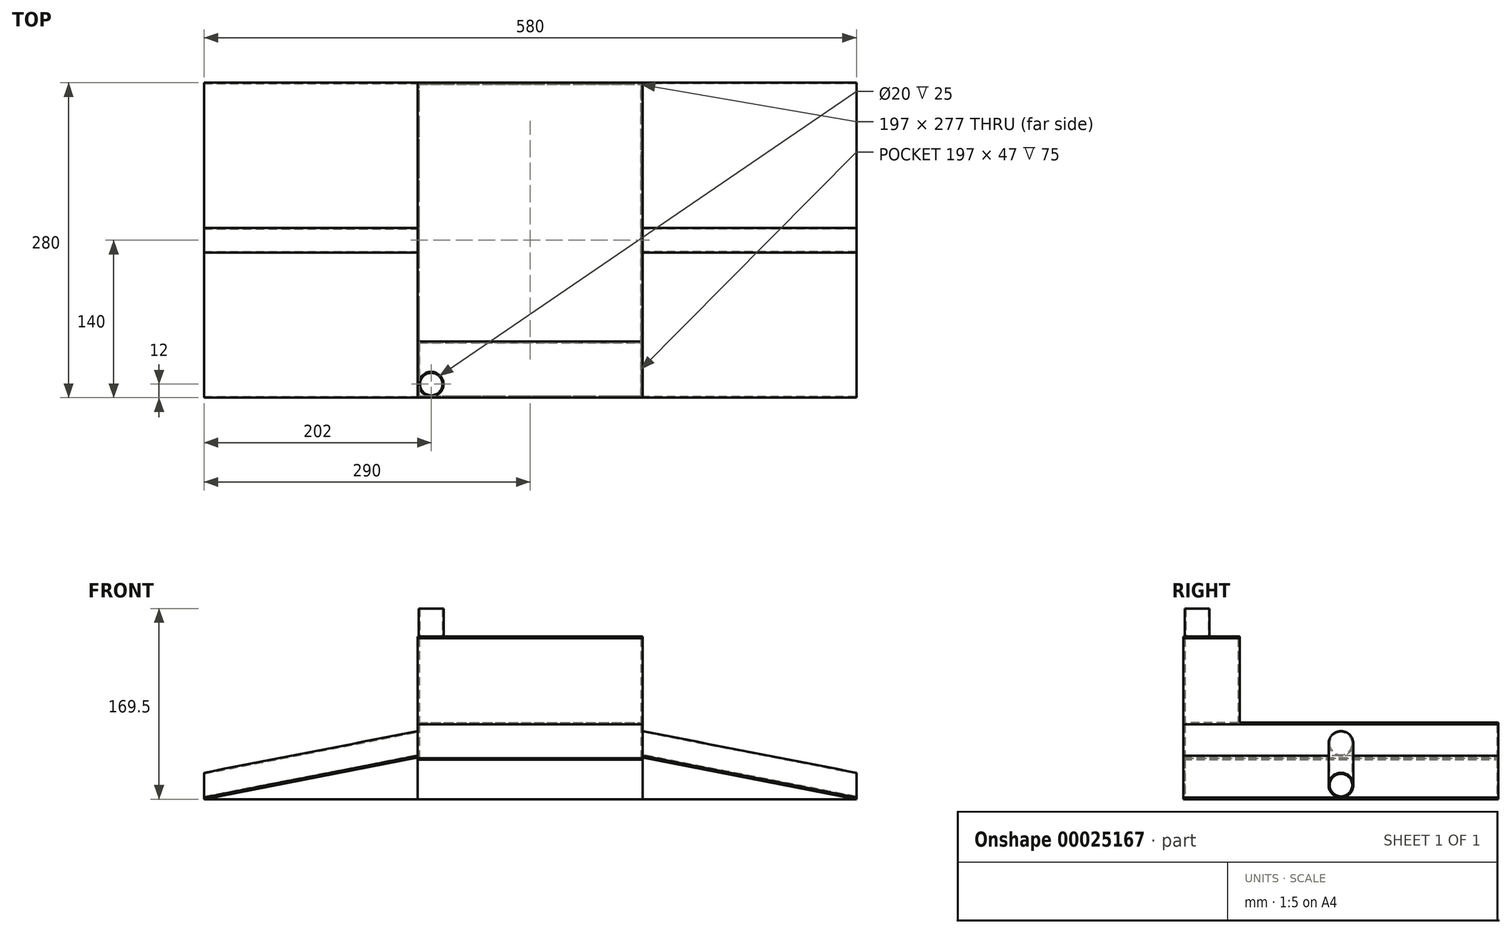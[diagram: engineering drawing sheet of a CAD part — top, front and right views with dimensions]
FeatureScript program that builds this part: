
annotation { "Feature Type Name" : "Feature", "Feature Type Description" : "" }
export const myFeature = defineFeature(function(context is Context, id is Id, definition is map)
    precondition{}
    {
        {
            var Q0;
            Q0=qCreatedBy(makeId("Top.planeOp"),FACE);
            var sketch = newSketch(context, id + "F0", { "sketchPlane" : qUnion([Q0])});
            skLineSegment(sketch, "E0.bottom", {"start": v(0, 0) * mm, "end": v(200, 0) * mm});
            skLineSegment(sketch, "E0.top", {"start": v(0, 280) * mm, "end": v(200, 280) * mm});
            skLineSegment(sketch, "E0.left", {"start": v(0, 0) * mm, "end": v(0, 280) * mm});
            skLineSegment(sketch, "E0.right", {"start": v(200, 0) * mm, "end": v(200, 280) * mm});
            skLineSegment(sketch, "E1.bottom", {"start": v(1.5, 278.5) * mm, "end": v(198.5, 278.5) * mm});
            skLineSegment(sketch, "E1.top", {"start": v(1.5, 1.5) * mm, "end": v(198.5, 1.5) * mm});
            skLineSegment(sketch, "E1.left", {"start": v(1.5, 278.5) * mm, "end": v(1.5, 1.5) * mm});
            skLineSegment(sketch, "E1.right", {"start": v(198.5, 278.5) * mm, "end": v(198.5, 1.5) * mm});
            skSolve(sketch);
        }
        {
            var Q0;
            Q0=makeQuery(id+"F0.imprint","IMPRINT",FACE,{"disambiguationData":[TD([[makeQuery(id+"F0.imprint","IMPRINT",EDGE,{"derivedFrom":sQuery(id+"F0.wireOp",EDGE,"E0.bottom")}),1.0]])]});
            extrude(context, id + "F1", {"entities" : qUnion([Q0]), "depth" : 35 * mm});
        }
        {
            var Q0;
            Q0=makeQuery(id+"F1.opExtrude","CAP_FACE",FACE,{"disambiguationData":[OSD([sQuery(id+"F0.wireOp",EDGE,"E0.bottom"),sQuery(id+"F0.wireOp",EDGE,"E0.top"),sQuery(id+"F0.wireOp",EDGE,"E0.left"),sQuery(id+"F0.wireOp",EDGE,"E0.right"),sQuery(id+"F0.wireOp",EDGE,"E1.bottom"),sQuery(id+"F0.wireOp",EDGE,"E1.top"),sQuery(id+"F0.wireOp",EDGE,"E1.left"),sQuery(id+"F0.wireOp",EDGE,"E1.right")])],"isStart":false});
            var sketch = newSketch(context, id + "F2", { "sketchPlane" : qUnion([Q0])});
            skLineSegment(sketch, "E2.bottom", {"start": v(0, 0) * mm, "end": v(200, 0) * mm});
            skLineSegment(sketch, "E2.top", {"start": v(0, 280) * mm, "end": v(200, 280) * mm});
            skLineSegment(sketch, "E2.left", {"start": v(0, 0) * mm, "end": v(0, 280) * mm});
            skLineSegment(sketch, "E2.right", {"start": v(200, 0) * mm, "end": v(200, 280) * mm});
            skSolve(sketch);
        }
        {
            var Q0;
            Q0=makeQuery(id+"F2.imprint","IMPRINT",FACE,{"disambiguationData":[TD([[makeQuery(id+"F2.imprint","IMPRINT",EDGE,{"derivedFrom":makeQuery(id+"F1.opExtrude","CAP_EDGE",EDGE,{"disambiguationData":[OSD([sQuery(id+"F0.wireOp",EDGE,"E1.bottom")])],"isStart":false})}),-1.0]])]});
            var Q1;
            Q1=makeQuery(id+"F2.imprint","IMPRINT",FACE,{"disambiguationData":[TD([[makeQuery(id+"F2.imprint","IMPRINT",EDGE,{"derivedFrom":sQuery(id+"F2.wireOp",EDGE,"E2.bottom")}),1.0]])]});
            extrude(context, id + "F3", {"entities" : qUnion([Q0, Q1]), "depth" : 1.5 * mm});
        }
        {
            var Q0;
            Q0=makeQuery(id+"F3.opExtrude","CAP_FACE",FACE,{"disambiguationData":[OSD([sQuery(id+"F2.wireOp",EDGE,"E2.bottom"),sQuery(id+"F2.wireOp",EDGE,"E2.top"),sQuery(id+"F2.wireOp",EDGE,"E2.left"),sQuery(id+"F2.wireOp",EDGE,"E2.right")])],"isStart":false});
            var sketch = newSketch(context, id + "F4", { "sketchPlane" : qUnion([Q0])});
            skLineSegment(sketch, "E3.bottom", {"start": v(200, 280) * mm, "end": v(0, 280) * mm});
            skLineSegment(sketch, "E3.top", {"start": v(200, 0) * mm, "end": v(0, 0) * mm});
            skLineSegment(sketch, "E3.left", {"start": v(200, 280) * mm, "end": v(200, 0) * mm});
            skLineSegment(sketch, "E3.right", {"start": v(0, 280) * mm, "end": v(0, 0) * mm});
            skLineSegment(sketch, "E4.bottom", {"start": v(1.5, 1.5) * mm, "end": v(198.5, 1.5) * mm});
            skLineSegment(sketch, "E4.top", {"start": v(1.5, 278.5) * mm, "end": v(198.5, 278.5) * mm});
            skLineSegment(sketch, "E4.left", {"start": v(1.5, 1.5) * mm, "end": v(1.5, 278.5) * mm});
            skLineSegment(sketch, "E4.right", {"start": v(198.5, 1.5) * mm, "end": v(198.5, 278.5) * mm});
            skSolve(sketch);
        }
        {
            var Q0;
            Q0 = qSketchRegion(id + "F4", true);
            extrude(context, id + "F5", {"entities" : qUnion([Q0]), "depth" : 30 * mm});
        }
        {
            var Q0;
            Q0=makeQuery(id+"F5.opExtrude","SWEPT_FACE",FACE,{"disambiguationData":[OSD([sQuery(id+"F4.wireOp",EDGE,"E3.right")])]});
            var sketch = newSketch(context, id + "F6", { "sketchPlane" : qUnion([Q0])});
            skLineSegment(sketch, "E5", {"start": v(-140, 36.5) * mm, "end": v(-140, 49.5) * mm});
            skCircle(sketch, "E6", {"center": v(-140, 49.5) * mm, "radius": 11 * mm});
            skCircle(sketch, "E7", {"center": v(-140, 49.5) * mm, "radius": 10 * mm});
            skSolve(sketch);
        }
        {
            var Q0;
            Q0=qCreatedBy(makeId("Front.planeOp"),FACE);
            cPlane(context, id + "F7", {"entities" : qUnion([Q0]), "cplaneType" : CPlaneType.OFFSET, "offset" : 140 * mm, "oppositeDirection" : true, "width" : 150 * mm, "height" : 150 * mm});
        }
        {
            var Q0;
            Q0=qCreatedBy(id+"F7.planeOp",FACE);
            var sketch = newSketch(context, id + "F8", { "sketchPlane" : qUnion([Q0])});
            skLineSegment(sketch, "E8", {"start": v(0, 0) * mm, "end": v(0, 49.5) * mm});
            skLineSegment(sketch, "E9", {"start": v(0, 49.5) * mm, "end": v(-190, 12.5) * mm});
            skLineSegment(sketch, "E10", {"start": v(-190, 12.5) * mm, "end": v(-10, 47.55) * mm});
            skSolve(sketch);
        }
        {
            var Q0;
            Q0=makeQuery(id+"F6.imprint","IMPRINT",FACE,{"disambiguationData":[TD([[makeQuery(id+"F6.imprint","IMPRINT",EDGE,{"derivedFrom":sQuery(id+"F6.wireOp",EDGE,"E6")}),1.0]])]});
            var Q1;
            Q1=sQuery(id+"F8.wireOp",EDGE,"E9");
            sweep(context, id + "F9", {"profiles" : qUnion([Q0]), "path" : qUnion([Q1])});
        }
        {
            var Q0;
            Q0=makeQuery(id+"F9.opSweep","CAP_FACE",FACE,{"disambiguationData":[OSD([sQuery(id+"F6.wireOp",EDGE,"E6"),sQuery(id+"F6.wireOp",EDGE,"E7"),sQuery(id+"F8.wireOp",VERTEX,"E9.end")])],"isStart":false});
            var sketch = newSketch(context, id + "F10", { "sketchPlane" : qUnion([Q0])});
            skLineSegment(sketch, "E11.bottom", {"start": v(-140, 1.5) * mm, "end": v(0, 1.5) * mm});
            skLineSegment(sketch, "E11.top", {"start": v(-140, 0) * mm, "end": v(0, 0) * mm});
            skLineSegment(sketch, "E11.right", {"start": v(0, 1.5) * mm, "end": v(0, 0) * mm});
            skLineSegment(sketch, "E12.bottom", {"start": v(-140, 1.5) * mm, "end": v(-280, 1.5) * mm});
            skLineSegment(sketch, "E12.top", {"start": v(-140, 0) * mm, "end": v(-280, 0) * mm});
            skLineSegment(sketch, "E12.right", {"start": v(-280, 1.5) * mm, "end": v(-280, 0) * mm});
            skSolve(sketch);
        }
        {
            var Q0;
            Q0=makeQuery(id+"F10.imprint","IMPRINT",FACE,{"disambiguationData":[TD([[makeQuery(id+"F10.imprint","IMPRINT",EDGE,{"derivedFrom":sQuery(id+"F10.wireOp",EDGE,"E11.bottom")}),-1.0]])]});
            var Q1;
            Q1=sQuery(id+"F8.wireOp",EDGE,"E9");
            sweep(context, id + "F11", {"profiles" : qUnion([Q0]), "path" : qUnion([Q1])});
        }
        {
            var Q0;
            Q0=qCreatedBy(makeId("Right.planeOp"),FACE);
            cPlane(context, id + "F12", {"entities" : qUnion([Q0]), "cplaneType" : CPlaneType.OFFSET, "offset" : 100 * mm, "width" : 150 * mm, "height" : 150 * mm});
        }
        {
            var Q0;
            Q0=makeQuery(id+"F11.opSweep","SWEPT_BODY",BODY,{"disambiguationData":[OSD([sQuery(id+"F6.wireOp",EDGE,"E6"),sQuery(id+"F8.wireOp",VERTEX,"E9.end"),sQuery(id+"F8.wireOp",EDGE,"E9"),sQuery(id+"F10.wireOp",EDGE,"bbc44509-5c85-48de-a6ec-72a2609fa2f3"),sQuery(id+"F10.wireOp",EDGE,"a9bd47df-7b8e-4d3d-8cbc-6e7aad29a798"),sQuery(id+"F10.wireOp",EDGE,"b129ef78-7b1a-4f70-9433-c68172c07502")])]});
            var Q1;
            Q1=makeQuery(id+"F9.opSweep","SWEPT_BODY",BODY,{"disambiguationData":[OSD([sQuery(id+"F6.wireOp",EDGE,"E6"),sQuery(id+"F6.wireOp",EDGE,"E7"),sQuery(id+"F8.wireOp",EDGE,"E9")])]});
            var Q2;
            Q2=makeQuery(id+"F11.opSweep","SWEPT_BODY",BODY,{"disambiguationData":[OSD([sQuery(id+"F6.wireOp",EDGE,"E6"),sQuery(id+"F8.wireOp",VERTEX,"E9.end"),sQuery(id+"F8.wireOp",EDGE,"E9"),sQuery(id+"F10.wireOp",EDGE,"c09ad4ab-e0c7-4d02-b4d3-9f80001b407e"),sQuery(id+"F10.wireOp",EDGE,"19dc77f5-9d7f-4f5a-aac5-f32d7d39baf3"),sQuery(id+"F10.wireOp",EDGE,"af366fa5-4e77-486b-961f-37b205b3a81b"),sQuery(id+"F10.wireOp",EDGE,"1364792c-ecac-41d2-8e04-122f8f5d8162")])]});
            var Q3;
            Q3=qCreatedBy(id+"F12.planeOp",FACE);
            mirror(context, id + "F13", {"entities" : qUnion([Q0, Q1, Q2]), "mirrorPlane" : qUnion([Q3])});
        }
        {
            var Q0;
            Q0=makeQuery(id+"F11.opSweep","SWEPT_FACE",FACE,{"disambiguationData":[OSD([sQuery(id+"F8.wireOp",EDGE,"E9"),sQuery(id+"F10.wireOp",EDGE,"E11.right")])]});
            var sketch = newSketch(context, id + "F14", { "sketchPlane" : qUnion([Q0])});
            skLineSegment(sketch, "E13", {"start": v(0, 37) * mm, "end": v(0, 0) * mm});
            skLineSegment(sketch, "E14", {"start": v(0, 0) * mm, "end": v(-190, 0) * mm});
            skLineSegment(sketch, "E15", {"start": v(-190, 0) * mm, "end": v(0, 37) * mm});
            skSolve(sketch);
        }
        {
            var Q0;
            Q0 = qSketchRegion(id + "F14", true);
            extrude(context, id + "F15", {"entities" : qUnion([Q0]), "oppositeDirection" : true, "depth" : 1 * mm});
        }
        {
            var Q0;
            Q0=makeQuery(id+"F15.opExtrude","SWEPT_BODY",BODY,{"disambiguationData":[OSD([sQuery(id+"F14.wireOp",EDGE,"E13"),sQuery(id+"F14.wireOp",EDGE,"E14"),sQuery(id+"F14.wireOp",EDGE,"E15")])]});
            var Q1;
            Q1=qCreatedBy(id+"F7.planeOp",FACE);
            mirror(context, id + "F16", {"entities" : qUnion([Q0]), "mirrorPlane" : qUnion([Q1])});
        }
        {
            var Q0;
            Q0=makeQuery(id+"F15.opExtrude","SWEPT_BODY",BODY,{"disambiguationData":[OSD([sQuery(id+"F14.wireOp",EDGE,"E13"),sQuery(id+"F14.wireOp",EDGE,"E14"),sQuery(id+"F14.wireOp",EDGE,"E15")])]});
            var Q1;
            Q1=makeQuery(id+"F16.opPattern","COPY",BODY,{"derivedFrom":makeQuery(id+"F15.opExtrude","SWEPT_BODY",BODY,{"disambiguationData":[OSD([sQuery(id+"F14.wireOp",EDGE,"E13"),sQuery(id+"F14.wireOp",EDGE,"E14"),sQuery(id+"F14.wireOp",EDGE,"E15")])]}),"instanceName":"1"});
            var Q2;
            Q2=qCreatedBy(id+"F12.planeOp",FACE);
            mirror(context, id + "F17", {"entities" : qUnion([Q0, Q1]), "mirrorPlane" : qUnion([Q2])});
        }
        {
            var Q0;
            Q0=makeQuery(id+"F1.opExtrude","CAP_FACE",FACE,{"disambiguationData":[OSD([sQuery(id+"F0.wireOp",EDGE,"E0.bottom"),sQuery(id+"F0.wireOp",EDGE,"E0.top"),sQuery(id+"F0.wireOp",EDGE,"E0.left"),sQuery(id+"F0.wireOp",EDGE,"E0.right"),sQuery(id+"F0.wireOp",EDGE,"E1.bottom"),sQuery(id+"F0.wireOp",EDGE,"E1.top"),sQuery(id+"F0.wireOp",EDGE,"E1.left"),sQuery(id+"F0.wireOp",EDGE,"E1.right")])],"isStart":true});
            var sketch = newSketch(context, id + "F18", { "sketchPlane" : qUnion([Q0])});
            skLineSegment(sketch, "E16", {"start": v(198.5, -278.5) * mm, "end": v(200, -278.5) * mm});
            skLineSegment(sketch, "E17", {"start": v(1.5, -278.5) * mm, "end": v(0, -278.5) * mm});
            skLineSegment(sketch, "E18", {"start": v(198.5, -1.5) * mm, "end": v(200, -1.5) * mm});
            skLineSegment(sketch, "E19", {"start": v(1.5, -1.5) * mm, "end": v(0, -1.5) * mm});
            skSolve(sketch);
        }
        {
            var Q0;
            {var subQ2=sQuery(id+"F18.wireOp",EDGE,"E16");Q0=makeQuery(id+"F18.imprint","IMPRINT",FACE,{"disambiguationData":[TD([[makeQuery(id+"F18.imprint","IMPRINT",EDGE,{"derivedFrom":subQ2}),1.0]])]});}
            var Q1;
            {var subQ2=sQuery(id+"F18.wireOp",EDGE,"E17");Q1=makeQuery(id+"F18.imprint","IMPRINT",FACE,{"disambiguationData":[TD([[makeQuery(id+"F18.imprint","IMPRINT",EDGE,{"derivedFrom":subQ2}),-1.0]])]});}
            extrude(context, id + "F19", {"entities" : qUnion([Q0, Q1]), "operationType" : NewBodyOperationType.REMOVE, "oppositeDirection" : true, "depth" : 35 * mm});
        }
        {
            var Q0;
            Q0=makeQuery(id+"F5.opExtrude","CAP_FACE",FACE,{"disambiguationData":[OSD([sQuery(id+"F4.wireOp",EDGE,"E3.bottom"),sQuery(id+"F4.wireOp",EDGE,"E3.top"),sQuery(id+"F4.wireOp",EDGE,"E3.left"),sQuery(id+"F4.wireOp",EDGE,"E3.right"),sQuery(id+"F4.wireOp",EDGE,"E4.bottom"),sQuery(id+"F4.wireOp",EDGE,"E4.top"),sQuery(id+"F4.wireOp",EDGE,"E4.left"),sQuery(id+"F4.wireOp",EDGE,"E4.right")])],"isStart":false});
            var sketch = newSketch(context, id + "F20", { "sketchPlane" : qUnion([Q0])});
            skLineSegment(sketch, "E20.bottom", {"start": v(200, 280) * mm, "end": v(0, 280) * mm});
            skLineSegment(sketch, "E20.top", {"start": v(200, 0) * mm, "end": v(0, 0) * mm});
            skLineSegment(sketch, "E20.left", {"start": v(200, 280) * mm, "end": v(200, 0) * mm});
            skLineSegment(sketch, "E20.right", {"start": v(0, 280) * mm, "end": v(0, 0) * mm});
            skSolve(sketch);
        }
        {
            var Q0;
            Q0=makeQuery(id+"F20.imprint","IMPRINT",FACE,{"disambiguationData":[TD([[makeQuery(id+"F20.imprint","IMPRINT",EDGE,{"derivedFrom":makeQuery(id+"F5.opExtrude","CAP_EDGE",EDGE,{"disambiguationData":[OSD([sQuery(id+"F4.wireOp",EDGE,"E4.bottom")])],"isStart":false})}),1.0]])]});
            var Q1;
            Q1=makeQuery(id+"F20.imprint","IMPRINT",FACE,{"disambiguationData":[TD([[makeQuery(id+"F20.imprint","IMPRINT",EDGE,{"derivedFrom":sQuery(id+"F20.wireOp",EDGE,"E20.bottom")}),-1.0]])]});
            extrude(context, id + "F21", {"entities" : qUnion([Q0, Q1]), "depth" : 1.5 * mm});
        }
        {
            var Q0;
            Q0=makeQuery(id+"F21.opExtrude","CAP_FACE",FACE,{"disambiguationData":[OSD([sQuery(id+"F20.wireOp",EDGE,"E20.bottom"),sQuery(id+"F20.wireOp",EDGE,"E20.top"),sQuery(id+"F20.wireOp",EDGE,"E20.left"),sQuery(id+"F20.wireOp",EDGE,"E20.right")])],"isStart":false});
            var sketch = newSketch(context, id + "F22", { "sketchPlane" : qUnion([Q0])});
            skLineSegment(sketch, "E21.bottom", {"start": v(0, 0) * mm, "end": v(200, 0) * mm});
            skLineSegment(sketch, "E21.top", {"start": v(0, 50) * mm, "end": v(200, 50) * mm});
            skLineSegment(sketch, "E21.left", {"start": v(0, 0) * mm, "end": v(0, 50) * mm});
            skLineSegment(sketch, "E21.right", {"start": v(200, 0) * mm, "end": v(200, 50) * mm});
            skLineSegment(sketch, "E22.bottom", {"start": v(1.5, 48.5) * mm, "end": v(198.5, 48.5) * mm});
            skLineSegment(sketch, "E22.top", {"start": v(1.5, 1.5) * mm, "end": v(198.5, 1.5) * mm});
            skLineSegment(sketch, "E22.left", {"start": v(1.5, 48.5) * mm, "end": v(1.5, 1.5) * mm});
            skLineSegment(sketch, "E22.right", {"start": v(198.5, 48.5) * mm, "end": v(198.5, 1.5) * mm});
            skSolve(sketch);
        }
        {
            var Q0;
            Q0 = qSketchRegion(id + "F22", true);
            extrude(context, id + "F23", {"entities" : qUnion([Q0]), "operationType" : NewBodyOperationType.ADD, "depth" : 75 * mm});
        }
        {
            var Q0;
            Q0=makeQuery(id+"F23.opExtrude","CAP_FACE",FACE,{"disambiguationData":[OSD([sQuery(id+"F22.wireOp",EDGE,"E21.bottom"),sQuery(id+"F22.wireOp",EDGE,"E21.top"),sQuery(id+"F22.wireOp",EDGE,"E21.left"),sQuery(id+"F22.wireOp",EDGE,"E21.right"),sQuery(id+"F22.wireOp",EDGE,"E22.bottom"),sQuery(id+"F22.wireOp",EDGE,"E22.top"),sQuery(id+"F22.wireOp",EDGE,"E22.left"),sQuery(id+"F22.wireOp",EDGE,"E22.right")])],"isStart":false});
            var sketch = newSketch(context, id + "F24", { "sketchPlane" : qUnion([Q0])});
            skLineSegment(sketch, "E23.bottom", {"start": v(0, 0) * mm, "end": v(200, 0) * mm});
            skLineSegment(sketch, "E23.top", {"start": v(0, 50) * mm, "end": v(200, 50) * mm});
            skLineSegment(sketch, "E23.left", {"start": v(0, 0) * mm, "end": v(0, 50) * mm});
            skLineSegment(sketch, "E23.right", {"start": v(200, 0) * mm, "end": v(200, 50) * mm});
            skSolve(sketch);
        }
        {
            var Q0;
            Q0=makeQuery(id+"F24.imprint","IMPRINT",FACE,{"disambiguationData":[TD([[makeQuery(id+"F24.imprint","IMPRINT",EDGE,{"derivedFrom":makeQuery(id+"F23.opExtrude","CAP_EDGE",EDGE,{"disambiguationData":[OSD([sQuery(id+"F22.wireOp",EDGE,"E22.bottom")])],"isStart":false})}),-1.0]])]});
            var Q1;
            Q1=makeQuery(id+"F24.imprint","IMPRINT",FACE,{"disambiguationData":[TD([[makeQuery(id+"F24.imprint","IMPRINT",EDGE,{"derivedFrom":sQuery(id+"F24.wireOp",EDGE,"E23.bottom")}),1.0]])]});
            extrude(context, id + "F25", {"entities" : qUnion([Q0, Q1]), "depth" : 1.5 * mm});
        }
        {
            var Q0;
            Q0=makeQuery(id+"F25.opExtrude","CAP_FACE",FACE,{"disambiguationData":[OSD([sQuery(id+"F24.wireOp",EDGE,"E23.bottom"),sQuery(id+"F24.wireOp",EDGE,"E23.top"),sQuery(id+"F24.wireOp",EDGE,"E23.left"),sQuery(id+"F24.wireOp",EDGE,"E23.right")])],"isStart":false});
            var sketch = newSketch(context, id + "F26", { "sketchPlane" : qUnion([Q0])});
            skCircle(sketch, "E24", {"center": v(12, 12) * mm, "radius": 11 * mm});
            skCircle(sketch, "E25", {"center": v(12, 12) * mm, "radius": 10 * mm});
            skSolve(sketch);
        }
        {
            var Q0;
            Q0 = qSketchRegion(id + "F26", true);
            extrude(context, id + "F27", {"entities" : qUnion([Q0]), "depth" : 25 * mm});
        }
    });
